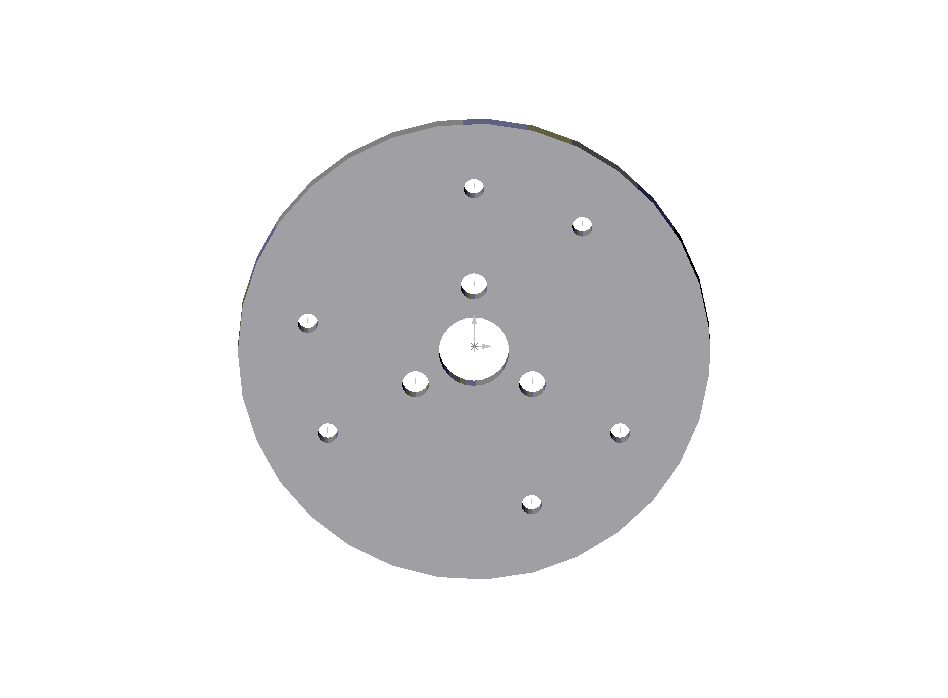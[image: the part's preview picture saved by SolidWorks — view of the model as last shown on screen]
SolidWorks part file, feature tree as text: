
SOLIDWORKS PART (.sldprt)
format: sldprt  version: not decoded by parser v0  size: 138,752 bytes
history: native  units: mm
features: sketch x4, pattern_circular x4, plane x3, cut_extrude x3, extrude x1 (+5 scaffold rows collapsed)
feature tree (20):
  scaffold x5  (default folders/planes/origin — collapsed)
  plane  "Plane1"
  plane  "Plane2"
  plane  "Plane3"
  sketch  "Sketch1"  dims[D1=70.0mm]
  extrude  "Base-Extrude"  Depth=3mm
  sketch  "Sketch2"  dims[D1=10.5mm]
  cut_extrude  "Cut-Extrude1"  [1 undecoded]
  sketch  "Sketch3"  dims[D1=4.0mm D2=10.0mm]
  cut_extrude  "Cut-Extrude3"  [1 undecoded]
  pattern_circular  "CirPattern1"  Count=3 Angle=360deg
  sketch  "Sketch4"  dims[D1=3.0mm D2=25.0mm]
  cut_extrude  "Cut-Extrude4"  [1 undecoded]
  pattern_circular  "CirPattern3"  Count=2 Angle=40deg
  pattern_circular  "CirPattern4"  Count=2 Angle=120deg
  pattern_circular  "CirPattern6"  Count=2 Angle=120deg
decode coverage: 9 of 12 modeling features carry decoded parameters
note: 3 parameter values undecoded
summary: no parameter record found for 3 features
note: suppression state not decoded; provenance and decode notes live in map.json
